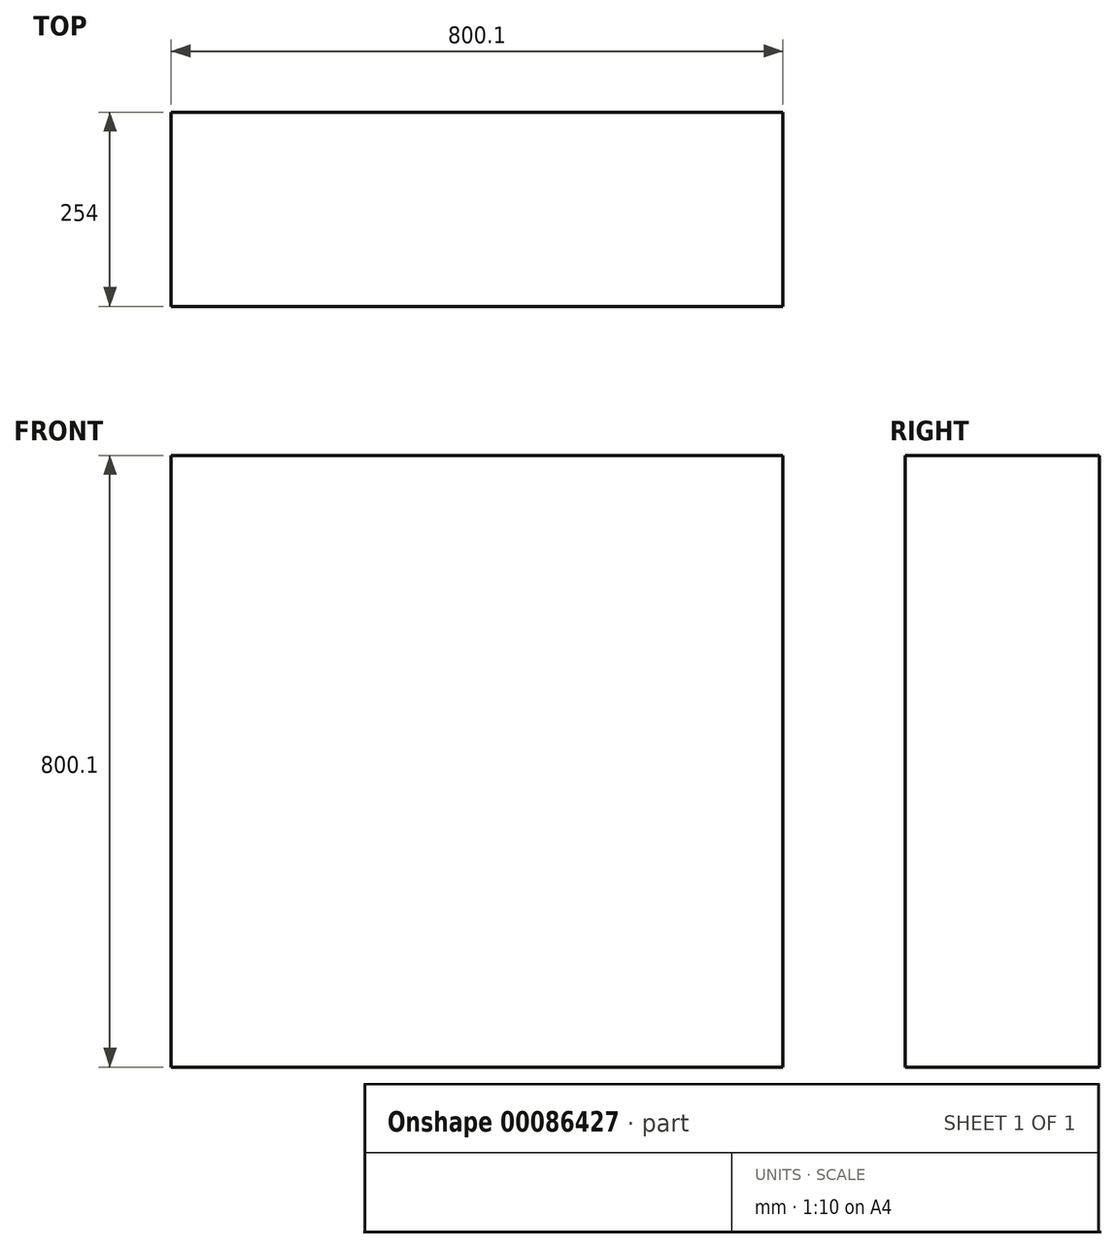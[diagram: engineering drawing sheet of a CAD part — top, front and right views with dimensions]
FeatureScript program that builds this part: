
annotation { "Feature Type Name" : "Feature", "Feature Type Description" : "" }
export const myFeature = defineFeature(function(context is Context, id is Id, definition is map)
    precondition{}
    {
        {
            var Q0;
            Q0=qCreatedBy(makeId("Front.planeOp"),FACE);
            var sketch = newSketch(context, id + "F0", { "sketchPlane" : qUnion([Q0])});
            skLineSegment(sketch, "E0.bottom", {"start": v(-400.05, 400.05) * mm, "end": v(400.05, 400.05) * mm});
            skLineSegment(sketch, "E0.top", {"start": v(-400.05, -400.05) * mm, "end": v(400.05, -400.05) * mm});
            skLineSegment(sketch, "E0.left", {"start": v(-400.05, 400.05) * mm, "end": v(-400.05, -400.05) * mm});
            skLineSegment(sketch, "E0.right", {"start": v(400.05, 400.05) * mm, "end": v(400.05, -400.05) * mm});
            skPoint(sketch, "E0.middle", {"position": v(0, 0) * mm});
            skSolve(sketch);
        }
        {
            var Q0;
            Q0=makeQuery(id+"F0.imprint","IMPRINT",FACE,{"disambiguationData":[TD([[makeQuery(id+"F0.imprint","IMPRINT",EDGE,{"derivedFrom":sQuery(id+"F0.wireOp",EDGE,"E0.bottom")}),-1.0]])]});
            extrude(context, id + "F1", {"entities" : qUnion([Q0]), "endBound" : BoundingType.SYMMETRIC, "depth" : 254 * mm});
        }
    });
